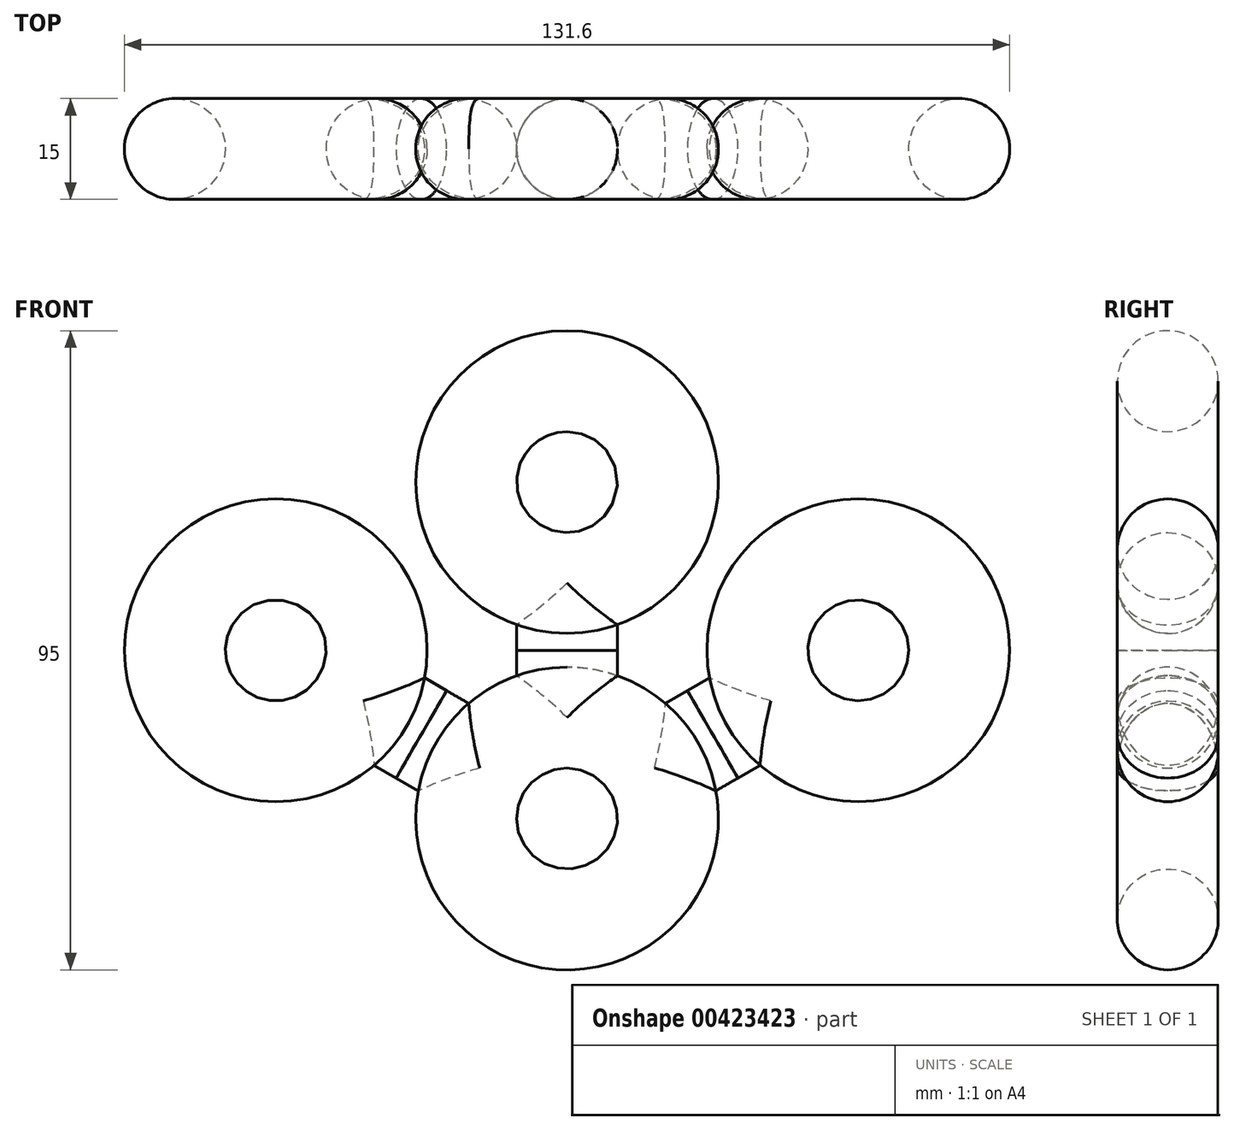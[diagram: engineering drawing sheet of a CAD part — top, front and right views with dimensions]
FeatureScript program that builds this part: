
annotation { "Feature Type Name" : "Feature", "Feature Type Description" : "" }
export const myFeature = defineFeature(function(context is Context, id is Id, definition is map)
    precondition{}
    {
        {
            var Q0;
            Q0=qCreatedBy(makeId("Top.planeOp"),FACE);
            cPlane(context, id + "F0", {"entities" : qUnion([Q0]), "cplaneType" : CPlaneType.OFFSET, "offset" : 50 * mm, "width" : 150 * mm, "height" : 150 * mm});
        }
        {
            var Q0;
            Q0=qCreatedBy(makeId("Top.planeOp"),FACE);
            cPlane(context, id + "F1", {"entities" : qUnion([Q0]), "cplaneType" : CPlaneType.OFFSET, "offset" : 25 * mm, "width" : 150 * mm, "height" : 150 * mm});
        }
        {
            var Q0;
            Q0=qCreatedBy(makeId("Front.planeOp"),FACE);
            var sketch = newSketch(context, id + "F2", { "sketchPlane" : qUnion([Q0])});
            skCircle(sketch, "E0", {"center": v(0, 0) * mm, "radius": 15 * mm});
            skLineSegment(sketch, "E1", {"start": v(0, 15) * mm, "end": v(0, 35) * mm});
            skCircle(sketch, "E2", {"center": v(0, 50) * mm, "radius": 15 * mm});
            skCircle(sketch, "E3", {"center": v(-43.3, 25) * mm, "radius": 15 * mm});
            skLineSegment(sketch, "E4", {"start": v(-30.31, 17.5) * mm, "end": v(-13, 7.5) * mm});
            skCircle(sketch, "E5.MirrorC", {"center": v(43.3, 25) * mm, "radius": 15 * mm});
            skLineSegment(sketch, "E6.MirrorCS", {"start": v(30.31, 17.5) * mm, "end": v(13, 7.5) * mm});
            skSolve(sketch);
        }
        {
            var Q0;
            Q0=qCreatedBy(makeId("Top.planeOp"),FACE);
            var sketch = newSketch(context, id + "F3", { "sketchPlane" : qUnion([Q0])});
            skCircle(sketch, "E7", {"center": v(-15, 0) * mm, "radius": 7.5 * mm});
            skSolve(sketch);
        }
        {
            var Q0;
            Q0=qCreatedBy(id+"F0.planeOp",FACE);
            var sketch = newSketch(context, id + "F4", { "sketchPlane" : qUnion([Q0])});
            skCircle(sketch, "E8", {"center": v(-15, 0) * mm, "radius": 7.5 * mm});
            skSolve(sketch);
        }
        {
            var Q0;
            Q0=qCreatedBy(id+"F1.planeOp",FACE);
            var sketch = newSketch(context, id + "F5", { "sketchPlane" : qUnion([Q0])});
            skCircle(sketch, "E9", {"center": v(0, 0) * mm, "radius": 7.5 * mm});
            skSolve(sketch);
        }
        {
            var Q0;
            Q0=qCreatedBy(makeId("Top.planeOp"),FACE);
            var sketch = newSketch(context, id + "F6", { "sketchPlane" : qUnion([Q0])});
            skLineSegment(sketch, "E10", {"start": v(0, 0) * mm, "end": v(0, -30.53) * mm});
            skSolve(sketch);
        }
        {
            var Q0;
            Q0=qCreatedBy(id+"F0.planeOp",FACE);
            var sketch = newSketch(context, id + "F7", { "sketchPlane" : qUnion([Q0])});
            skLineSegment(sketch, "E11", {"start": v(0, 0) * mm, "end": v(0, -33.98) * mm});
            skSolve(sketch);
        }
        {
            var Q0;
            Q0=makeQuery(id+"F3.imprint","IMPRINT",FACE,{"disambiguationData":[TD([[makeQuery(id+"F3.imprint","IMPRINT",EDGE,{"derivedFrom":sQuery(id+"F3.wireOp",EDGE,"E7")}),1.0]])]});
            var Q1;
            Q1=sQuery(id+"F3.wireOp",EDGE,"E7");
            var Q2;
            Q2=sQuery(id+"F6.wireOp",EDGE,"E10");
            var Q3;
            Q3=sQuery(id+"F6.wireOp",EDGE,"E10");
            revolve(context, id + "F8", {"entities" : qUnion([Q0]), "surfaceEntities" : qUnion([Q1, Q2]), "axis" : qUnion([Q3]), "revolveType" : RevolveType.FULL});
        }
        {
            var Q0;
            Q0=makeQuery(id+"F4.imprint","IMPRINT",FACE,{"disambiguationData":[TD([[makeQuery(id+"F4.imprint","IMPRINT",EDGE,{"derivedFrom":sQuery(id+"F4.wireOp",EDGE,"E8")}),1.0]])]});
            var Q1;
            Q1=sQuery(id+"F7.wireOp",EDGE,"E11");
            revolve(context, id + "F9", {"entities" : qUnion([Q0]), "axis" : qUnion([Q1]), "revolveType" : RevolveType.FULL});
        }
        {
            var Q0;
            Q0=makeQuery(id+"F5.imprint","IMPRINT",FACE,{"disambiguationData":[TD([[makeQuery(id+"F5.imprint","IMPRINT",EDGE,{"derivedFrom":sQuery(id+"F5.wireOp",EDGE,"E9")}),1.0]])]});
            var Q1;
            Q1=sQuery(id+"F5.wireOp",EDGE,"E9");
            var Q2;
            Q2=makeQuery(id+"F8.opRevolve","SWEPT_BODY",BODY,{"disambiguationData":[OSD([sQuery(id+"F3.wireOp",EDGE,"E7")])]});
            extrude(context, id + "F10", {"entities" : qUnion([Q0]), "surfaceEntities" : qUnion([Q1]), "endBound" : BoundingType.UP_TO_BODY, "oppositeDirection" : true, "endBoundEntityBody" : qUnion([Q2]), "depth" : 25 * mm});
        }
        {
            var Q0;
            Q0=makeQuery(id+"F10.opExtrude","CAP_FACE",FACE,{"disambiguationData":[OSD([sQuery(id+"F5.wireOp",EDGE,"E9")])],"isStart":true});
            var Q1;
            Q1=makeQuery(id+"F9.opRevolve","SWEPT_BODY",BODY,{"disambiguationData":[OSD([sQuery(id+"F4.wireOp",EDGE,"E8")])]});
            extrude(context, id + "F11", {"entities" : qUnion([Q0]), "endBound" : BoundingType.UP_TO_BODY, "endBoundEntityBody" : qUnion([Q1]), "depth" : 25 * mm});
        }
        {
            var Q0;
            Q0=makeQuery(id+"F11.opExtrude","SWEPT_BODY",BODY,{"disambiguationData":[OSD([sQuery(id+"F5.wireOp",EDGE,"E9")])]});
            var Q1;
            Q1=makeQuery(id+"F10.opExtrude","SWEPT_BODY",BODY,{"disambiguationData":[OSD([sQuery(id+"F5.wireOp",EDGE,"E9")])]});
            var Q2;
            Q2=makeQuery(id+"F9.opRevolve","SWEPT_BODY",BODY,{"disambiguationData":[OSD([sQuery(id+"F4.wireOp",EDGE,"E8")])]});
            var Q3;
            Q3=sQuery(id+"F6.wireOp",EDGE,"E10");
            circularPattern(context, id + "F12", {"entities" : qUnion([Q0, Q1, Q2]), "axis" : qUnion([Q3]), "angle" : 60 * degree, "instanceCount" : 2, "oppositeDirection" : true, "equalSpace" : true, "isCentered" : true});
        }
    });
